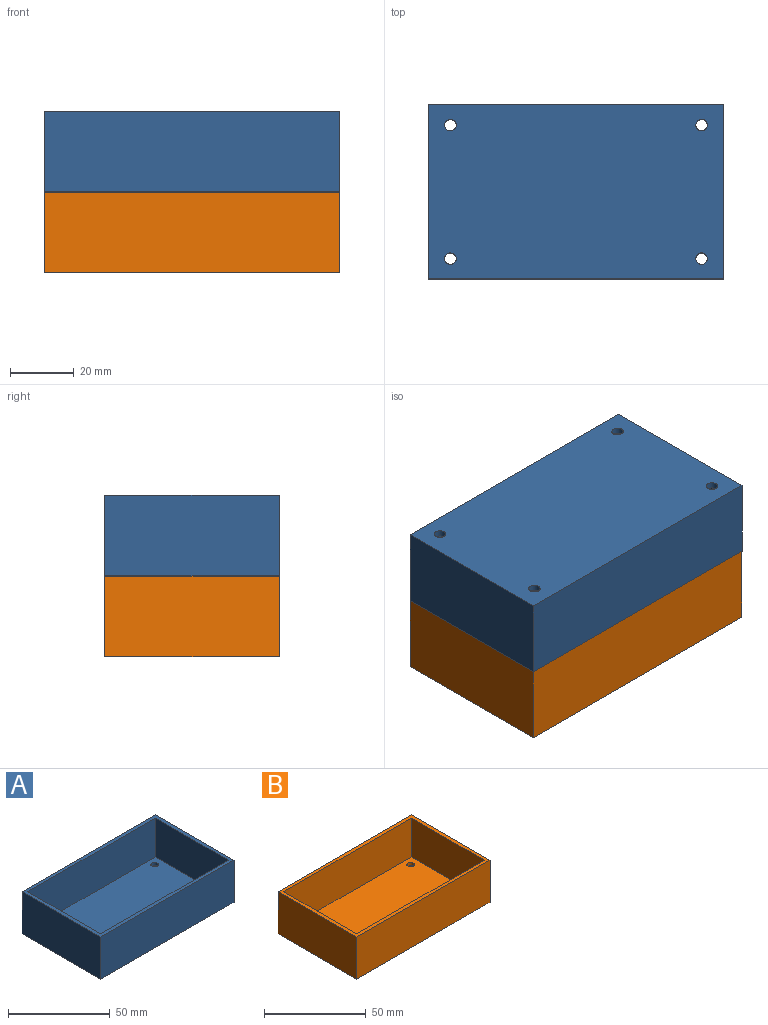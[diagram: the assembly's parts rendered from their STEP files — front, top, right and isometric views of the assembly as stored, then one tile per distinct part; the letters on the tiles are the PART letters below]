
ASSEMBLY  parts=2 mates=1
PART A: 15 faces, bbox 92.9x54.8x25.4 mm
  f0: plane 54.8x25.4mm, normal (-1,0,0), area 1391.9mm2, adj f1,f6,f9,f14
  f1: plane 92.9x25.4mm, normal (0,-1,0), area 2359.7mm2, adj f0,f2,f9,f14
  f2: plane 54.8x25.4mm, normal (1,0,0), area 1391.9mm2, adj f1,f6,f9,f14
  f3: cylinder r=1.8mm len=3.61mm, axis (0,0,-1), area 22.7mm2, adj f8,f9
  f4: cylinder r=1.8mm len=3.61mm, axis (0,0,-1), area 22.7mm2, adj f8,f9
  f5: cylinder r=1.8mm len=3.61mm, axis (0,0,-1), area 22.7mm2, adj f8,f9
  f6: plane 92.9x25.4mm, normal (0,1,0), area 2359.7mm2, adj f0,f2,f9,f14
  f7: cylinder r=1.8mm len=3.61mm, axis (0,0,-1), area 22.7mm2, adj f8,f9
  f8: plane 88.9x50.8mm, normal (0,0,1), area 4475.3mm2, adj f3,f4,f5,f7,f10,f11,f12,f13
  f9: plane 92.9x54.8mm, normal (0,0,-1), area 5050.1mm2, adj f0,f1,f2,f3,f4,f5,f6,f7
  f10: plane 88.9x23.4mm, normal (0,-1,0), area 2080.3mm2, adj f8,f11,f13,f14
  f11: plane 50.8x23.4mm, normal (-1,0,0), area 1188.7mm2, adj f8,f10,f12,f14
  f12: plane 88.9x23.4mm, normal (0,1,0), area 2080.3mm2, adj f8,f11,f13,f14
  f13: plane 50.8x23.4mm, normal (1,0,0), area 1188.7mm2, adj f8,f10,f12,f14
  f14: plane 92.9x54.8mm, normal (0,0,1), area 574.8mm2, adj f0,f1,f2,f6,f10,f11,f12,f13
PART B: 15 faces, bbox 92.9x54.8x25.4 mm
  f0: plane 54.8x25.4mm, normal (-1,0,0), area 1391.9mm2, adj f1,f3,f5,f14
  f1: plane 92.9x25.4mm, normal (0,-1,0), area 2359.7mm2, adj f0,f2,f5,f14
  f2: plane 54.8x25.4mm, normal (1,0,0), area 1391.9mm2, adj f1,f3,f5,f14
  f3: plane 92.9x25.4mm, normal (0,1,0), area 2359.7mm2, adj f0,f2,f5,f14
  f4: plane 88.9x50.8mm, normal (0,0,1), area 4475.3mm2, adj f6,f7,f8,f9,f10,f11,f12,f13
  f5: plane 92.9x54.8mm, normal (0,0,-1), area 5050.1mm2, adj f0,f1,f2,f3,f6,f7,f8,f9
  f6: cylinder r=1.8mm len=3.61mm, axis (0,0,-1), area 22.7mm2, adj f4,f5
  f7: cylinder r=1.8mm len=3.61mm, axis (0,0,-1), area 22.7mm2, adj f4,f5
  f8: cylinder r=1.8mm len=3.61mm, axis (0,0,-1), area 22.7mm2, adj f4,f5
  f9: cylinder r=1.8mm len=3.61mm, axis (0,0,-1), area 22.7mm2, adj f4,f5
  f10: plane 88.9x23.4mm, normal (0,1,0), area 2080.3mm2, adj f4,f11,f13,f14
  f11: plane 50.8x23.4mm, normal (1,0,0), area 1188.7mm2, adj f4,f10,f12,f14
  f12: plane 88.9x23.4mm, normal (0,-1,0), area 2080.3mm2, adj f4,f11,f13,f14
  f13: plane 50.8x23.4mm, normal (-1,0,0), area 1188.7mm2, adj f4,f10,f12,f14
  f14: plane 92.9x54.8mm, normal (0,0,1), area 574.8mm2, adj f0,f1,f2,f3,f10,f11,f12,f13
PLACE A rot(axis=(1,0,0),180deg) t=(-11.69,-50.16,76.85)mm
PLACE B t=(-95.72,-57.22,26.05)mm
MATE fastened A.f14 <-> B.f14  axis (0,0,-1) through (-64.88,42.59,51.45)mm
